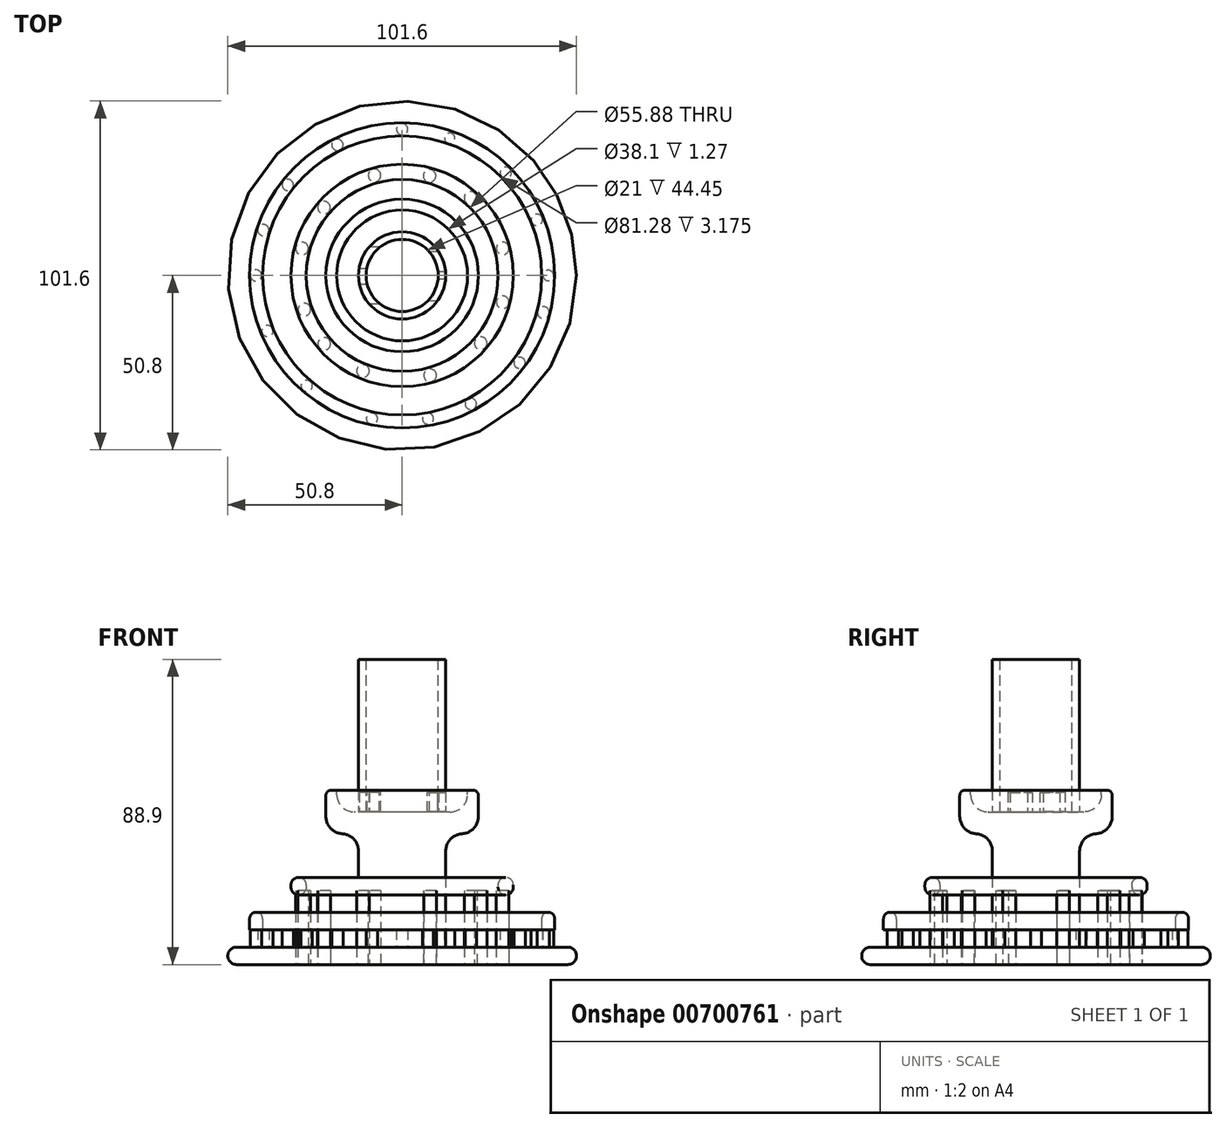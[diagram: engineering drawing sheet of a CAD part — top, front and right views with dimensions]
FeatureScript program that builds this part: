
annotation { "Feature Type Name" : "Feature", "Feature Type Description" : "" }
export const myFeature = defineFeature(function(context is Context, id is Id, definition is map)
    precondition{}
    {
        {
            var Q0;
            Q0=qCreatedBy(makeId("Top.planeOp"),FACE);
            var sketch = newSketch(context, id + "F0", { "sketchPlane" : qUnion([Q0])});
            skCircle(sketch, "E0", {"center": v(0, 0) * mm, "radius": 50.8 * mm});
            skSolve(sketch);
        }
        {
            var Q0;
            Q0 = qSketchRegion(id + "F0", true);
            extrude(context, id + "F1", {"entities" : qUnion([Q0]), "depth" : 5.08 * mm, "offsetDistance" : 25.4 * mm});
        }
        {
            var Q0;
            Q0=makeQuery(id+"F1.opExtrude","SWEPT_FACE",FACE,{"disambiguationData":[OSD([sQuery(id+"F0.wireOp",EDGE,"E0")])]});
            fillet(context, id + "F2", {"entities" : qUnion([Q0]), "radius" : 2.54 * mm, "tangentPropagation" : true, "allowEdgeOverflow" : false});
        }
        {
            var Q0;
            Q0=qCreatedBy(makeId("Top.planeOp"),FACE);
            var sketch = newSketch(context, id + "F3", { "sketchPlane" : qUnion([Q0])});
            skCircle(sketch, "E1", {"center": v(0, 0) * mm, "radius": 12.7 * mm});
            skSolve(sketch);
        }
        {
            var Q0;
            Q0 = qSketchRegion(id + "F3", true);
            extrude(context, id + "F4", {"entities" : qUnion([Q0]), "operationType" : NewBodyOperationType.ADD, "depth" : 88.9 * mm, "offsetDistance" : 25.4 * mm});
        }
        {
            var Q0;
            Q0=qCreatedBy(makeId("Top.planeOp"),FACE);
            var sketch = newSketch(context, id + "F5", { "sketchPlane" : qUnion([Q0])});
            skCircle(sketch, "E2", {"center": v(0, 0) * mm, "radius": 22.23 * mm});
            skSolve(sketch);
        }
        {
            var Q0;
            Q0 = qSketchRegion(id + "F5", true);
            extrude(context, id + "F6", {"entities" : qUnion([Q0]), "operationType" : NewBodyOperationType.ADD, "depth" : 50.8 * mm, "offsetDistance" : 25.4 * mm, "hasSecondDirection" : true, "secondDirectionOppositeDirection" : false, "secondDirectionDepth" : 38.1 * mm});
        }
        {
            var Q0;
            Q0=makeQuery(id+"F6.opExtrude","CAP_EDGE",EDGE,{"disambiguationData":[OSD([sQuery(id+"F5.wireOp",EDGE,"E2")])],"isStart":true});
            fillet(context, id + "F7", {"entities" : qUnion([Q0]), "radius" : 5.08 * mm, "tangentPropagation" : true, "allowEdgeOverflow" : false});
        }
        {
            var Q0;
            Q0=makeQuery(id+"F6.opExtrude","CAP_FACE",FACE,{"disambiguationData":[OSD([sQuery(id+"F5.wireOp",EDGE,"E2")])],"isStart":false});
            var sketch = newSketch(context, id + "F8", { "sketchPlane" : qUnion([Q0])});
            skCircle(sketch, "E3", {"center": v(0, 0) * mm, "radius": 12.7 * mm});
            skCircle(sketch, "E4", {"center": v(0, 0) * mm, "radius": 19.05 * mm});
            skSolve(sketch);
        }
        {
            var Q0;
            Q0 = qSketchRegion(id + "F8", true);
            extrude(context, id + "F9", {"entities" : qUnion([Q0]), "operationType" : NewBodyOperationType.REMOVE, "oppositeDirection" : true, "depth" : 6.35 * mm, "offsetDistance" : 25.4 * mm});
        }
        {
            var Q0;
            Q0=makeQuery(id+"F9.boolean.opBoolean","COPY",EDGE,{"derivedFrom":makeQuery(id+"F9.opExtrude","CAP_EDGE",EDGE,{"disambiguationData":[OSD([sQuery(id+"F8.wireOp",EDGE,"E4")])],"isStart":false})});
            fillet(context, id + "F10", {"entities" : qUnion([Q0]), "radius" : 5.08 * mm, "tangentPropagation" : true, "allowEdgeOverflow" : false});
        }
        {
            var Q0;
            Q0=qCreatedBy(makeId("Right.planeOp"),FACE);
            var sketch = newSketch(context, id + "F11", { "sketchPlane" : qUnion([Q0])});
            skLineSegment(sketch, "E5.bottom", {"start": v(-8.18, 44.59) * mm, "end": v(-2.47, 44.59) * mm});
            skLineSegment(sketch, "E5.top", {"start": v(-8.18, 50.22) * mm, "end": v(-2.47, 50.22) * mm});
            skLineSegment(sketch, "E5.left", {"start": v(-8.18, 44.59) * mm, "end": v(-8.18, 50.22) * mm});
            skLineSegment(sketch, "E5.right", {"start": v(-2.47, 44.59) * mm, "end": v(-2.47, 50.22) * mm});
            skLineSegment(sketch, "E6.bottom", {"start": v(2.09, 50.22) * mm, "end": v(8.4, 50.22) * mm});
            skLineSegment(sketch, "E6.top", {"start": v(2.09, 44.67) * mm, "end": v(8.4, 44.67) * mm});
            skLineSegment(sketch, "E6.left", {"start": v(2.09, 50.22) * mm, "end": v(2.09, 44.67) * mm});
            skLineSegment(sketch, "E6.right", {"start": v(8.4, 50.22) * mm, "end": v(8.4, 44.67) * mm});
            skSolve(sketch);
        }
        {
            var Q0;
            Q0 = qSketchRegion(id + "F11", true);
            extrude(context, id + "F12", {"entities" : qUnion([Q0]), "operationType" : NewBodyOperationType.REMOVE, "oppositeDirection" : true, "depth" : 12.7 * mm, "offsetDistance" : 25.4 * mm});
        }
        {
            var Q0;
            Q0=qCreatedBy(makeId("Right.planeOp"),FACE);
            var sketch = newSketch(context, id + "F13", { "sketchPlane" : qUnion([Q0])});
            skLineSegment(sketch, "E7.bottom", {"start": v(-7.5, 44.52) * mm, "end": v(-1.1, 44.52) * mm});
            skLineSegment(sketch, "E7.top", {"start": v(-7.5, 50.15) * mm, "end": v(-1.1, 50.15) * mm});
            skLineSegment(sketch, "E7.left", {"start": v(-7.5, 44.52) * mm, "end": v(-7.5, 50.15) * mm});
            skLineSegment(sketch, "E7.right", {"start": v(-1.1, 44.52) * mm, "end": v(-1.1, 50.15) * mm});
            skLineSegment(sketch, "E8.bottom", {"start": v(1.04, 50.15) * mm, "end": v(6.86, 50.15) * mm});
            skLineSegment(sketch, "E8.top", {"start": v(1.04, 44.54) * mm, "end": v(6.86, 44.54) * mm});
            skLineSegment(sketch, "E8.left", {"start": v(1.04, 50.15) * mm, "end": v(1.04, 44.54) * mm});
            skLineSegment(sketch, "E8.right", {"start": v(6.86, 50.15) * mm, "end": v(6.86, 44.54) * mm});
            skSolve(sketch);
        }
        {
            var Q0;
            Q0 = qSketchRegion(id + "F13", true);
            extrude(context, id + "F14", {"entities" : qUnion([Q0]), "operationType" : NewBodyOperationType.REMOVE, "depth" : 12.7 * mm, "offsetDistance" : 25.4 * mm});
        }
        {
            var Q0;
            Q0=makeQuery(id+"F4.opExtrude","CAP_FACE",FACE,{"disambiguationData":[OSD([sQuery(id+"F3.wireOp",EDGE,"E1")])],"isStart":false});
            var sketch = newSketch(context, id + "F15", { "sketchPlane" : qUnion([Q0])});
            skCircle(sketch, "E9", {"center": v(0, 0) * mm, "radius": 10.5 * mm});
            skSolve(sketch);
        }
        {
            var Q0;
            Q0 = qSketchRegion(id + "F15", true);
            extrude(context, id + "F16", {"entities" : qUnion([Q0]), "operationType" : NewBodyOperationType.REMOVE, "oppositeDirection" : true, "depth" : 44.45 * mm, "offsetDistance" : 25.4 * mm});
        }
        {
            var Q0;
            Q0=makeQuery(id+"F9.boolean.opBoolean","COPY",EDGE,{"derivedFrom":makeQuery(id+"F9.opExtrude","CAP_EDGE",EDGE,{"disambiguationData":[OSD([sQuery(id+"F8.wireOp",EDGE,"E4")])],"isStart":true})});
            var Q1;
            Q1=makeQuery(id+"F6.opExtrude","CAP_EDGE",EDGE,{"disambiguationData":[OSD([sQuery(id+"F5.wireOp",EDGE,"E2")])],"isStart":false});
            fillet(context, id + "F17", {"entities" : qUnion([Q0, Q1]), "radius" : 1.57 * mm, "tangentPropagation" : true, "allowEdgeOverflow" : false});
        }
        {
            var Q0;
            Q0=qCreatedBy(makeId("Top.planeOp"),FACE);
            var sketch = newSketch(context, id + "F18", { "sketchPlane" : qUnion([Q0])});
            skCircle(sketch, "E10", {"center": v(0, 0) * mm, "radius": 32.39 * mm});
            skCircle(sketch, "E11", {"center": v(0, 0) * mm, "radius": 27.94 * mm});
            skSolve(sketch);
        }
        {
            var Q0;
            Q0 = qSketchRegion(id + "F18", true);
            extrude(context, id + "F19", {"entities" : qUnion([Q0]), "depth" : 25.4 * mm, "offsetDistance" : 25.4 * mm, "hasSecondDirection" : true, "secondDirectionOppositeDirection" : false, "secondDirectionDepth" : 20.32 * mm});
        }
        {
            var Q0;
            Q0=makeQuery(id+"F19.opExtrude","CAP_EDGE",EDGE,{"disambiguationData":[OSD([sQuery(id+"F18.wireOp",EDGE,"E11")])],"isStart":false});
            var Q1;
            Q1=makeQuery(id+"F19.opExtrude","CAP_FACE",FACE,{"disambiguationData":[OSD([sQuery(id+"F18.wireOp",EDGE,"E10"),sQuery(id+"F18.wireOp",EDGE,"E11")])],"isStart":false});
            var Q2;
            Q2=makeQuery(id+"F19.opExtrude","CAP_EDGE",EDGE,{"disambiguationData":[OSD([sQuery(id+"F18.wireOp",EDGE,"E10")])],"isStart":false});
            var Q3;
            Q3=makeQuery(id+"F19.opExtrude","CAP_EDGE",EDGE,{"disambiguationData":[OSD([sQuery(id+"F18.wireOp",EDGE,"E11")])],"isStart":true});
            var Q4;
            Q4=makeQuery(id+"F19.opExtrude","CAP_EDGE",EDGE,{"disambiguationData":[OSD([sQuery(id+"F18.wireOp",EDGE,"E10")])],"isStart":true});
            fillet(context, id + "F20", {"entities" : qUnion([Q0, Q1, Q2, Q3, Q4]), "radius" : 2.22 * mm, "tangentPropagation" : true, "allowEdgeOverflow" : false});
        }
        {
            var Q0;
            Q0=qCreatedBy(makeId("Top.planeOp"),FACE);
            var sketch = newSketch(context, id + "F21", { "sketchPlane" : qUnion([Q0])});
            skCircle(sketch, "E12", {"center": v(-11.4, -27.8) * mm, "radius": 1.84 * mm});
            skCircle(sketch, "E13", {"center": v(8.15, -29.1) * mm, "radius": 1.84 * mm});
            skCircle(sketch, "E14", {"center": v(22.88, -19.7) * mm, "radius": 1.84 * mm});
            skCircle(sketch, "E15", {"center": v(-22.7, -19.9) * mm, "radius": 1.84 * mm});
            skCircle(sketch, "E16", {"center": v(29.3, -7.8) * mm, "radius": 1.84 * mm});
            skCircle(sketch, "E17", {"center": v(29.3, 7.87) * mm, "radius": 1.84 * mm});
            skCircle(sketch, "E18", {"center": v(19.9, 22.6) * mm, "radius": 1.84 * mm});
            skCircle(sketch, "E19", {"center": v(8, 29.01) * mm, "radius": 1.84 * mm});
            skCircle(sketch, "E20", {"center": v(-8.05, 29.15) * mm, "radius": 1.84 * mm});
            skCircle(sketch, "E21", {"center": v(-22.77, 19.75) * mm, "radius": 1.84 * mm});
            skCircle(sketch, "E22", {"center": v(-29.18, 7.85) * mm, "radius": 1.84 * mm});
            skCircle(sketch, "E23", {"center": v(-28.5, -9.94) * mm, "radius": 1.84 * mm});
            skSolve(sketch);
        }
        {
            var Q0;
            Q0 = qSketchRegion(id + "F21", true);
            extrude(context, id + "F22", {"entities" : qUnion([Q0]), "depth" : 21.59 * mm, "offsetDistance" : 25.4 * mm});
        }
        {
            var Q0;
            Q0=qCreatedBy(makeId("Top.planeOp"),FACE);
            var sketch = newSketch(context, id + "F23", { "sketchPlane" : qUnion([Q0])});
            skCircle(sketch, "E24", {"center": v(0, 0) * mm, "radius": 40.64 * mm});
            skCircle(sketch, "E25", {"center": v(0, 0) * mm, "radius": 44.45 * mm});
            skSolve(sketch);
        }
        {
            var Q0;
            Q0 = qSketchRegion(id + "F23", true);
            extrude(context, id + "F24", {"entities" : qUnion([Q0]), "depth" : 15.24 * mm, "offsetDistance" : 25.4 * mm, "hasSecondDirection" : true, "secondDirectionOppositeDirection" : false, "secondDirectionDepth" : 10.16 * mm});
        }
        {
            var Q0;
            Q0=makeQuery(id+"F24.opExtrude","CAP_EDGE",EDGE,{"disambiguationData":[OSD([sQuery(id+"F23.wireOp",EDGE,"E24")])],"isStart":false});
            var Q1;
            Q1=makeQuery(id+"F24.opExtrude","CAP_EDGE",EDGE,{"disambiguationData":[OSD([sQuery(id+"F23.wireOp",EDGE,"E25")])],"isStart":false});
            fillet(context, id + "F25", {"entities" : qUnion([Q0, Q1]), "radius" : 1.9 * mm, "tangentPropagation" : true, "allowEdgeOverflow" : false});
        }
        {
            var Q0;
            Q0=qCreatedBy(makeId("Top.planeOp"),FACE);
            var sketch = newSketch(context, id + "F26", { "sketchPlane" : qUnion([Q0])});
            skCircle(sketch, "E26", {"center": v(-18.86, 38.03) * mm, "radius": 1.65 * mm});
            skCircle(sketch, "E27", {"center": v(0, 42.6) * mm, "radius": 1.65 * mm});
            skCircle(sketch, "E28", {"center": v(-33.32, 26.35) * mm, "radius": 1.65 * mm});
            skCircle(sketch, "E29", {"center": v(-40.45, 13.2) * mm, "radius": 1.65 * mm});
            skCircle(sketch, "E30", {"center": v(-42.6, 0) * mm, "radius": 1.65 * mm});
            skCircle(sketch, "E31", {"center": v(-39.26, -16.16) * mm, "radius": 1.65 * mm});
            skCircle(sketch, "E32", {"center": v(-27.8, -32.16) * mm, "radius": 1.65 * mm});
            skCircle(sketch, "E33", {"center": v(-8.8, -41.71) * mm, "radius": 1.65 * mm});
            skCircle(sketch, "E34", {"center": v(19.99, -37.4) * mm, "radius": 1.65 * mm});
            skCircle(sketch, "E35", {"center": v(34.2, -25.44) * mm, "radius": 1.65 * mm});
            skCircle(sketch, "E36", {"center": v(13.86, 39.93) * mm, "radius": 1.52 * mm});
            skCircle(sketch, "E37", {"center": v(30.18, 29.92) * mm, "radius": 1.65 * mm});
            skCircle(sketch, "E38", {"center": v(39.24, 16.19) * mm, "radius": 1.67 * mm});
            skCircle(sketch, "E39", {"center": v(42.6, 0) * mm, "radius": 1.55 * mm});
            skCircle(sketch, "E40", {"center": v(41.12, -10.77) * mm, "radius": 1.72 * mm});
            skCircle(sketch, "E41", {"center": v(7.52, -41.7) * mm, "radius": 1.62 * mm});
            skSolve(sketch);
        }
        {
            var Q0;
            Q0 = qSketchRegion(id + "F26", true);
            extrude(context, id + "F27", {"entities" : qUnion([Q0]), "depth" : 10.16 * mm, "offsetDistance" : 25.4 * mm, "hasSecondDirection" : true, "secondDirectionOppositeDirection" : false, "secondDirectionDepth" : 5.08 * mm});
        }
        {
            var Q0;
            Q0=makeQuery(id+"F6.boolean.opBoolean","INTERSECT",EDGE,{"derivedFrom":[makeQuery(id+"F4.opExtrude","SWEPT_FACE",FACE,{"disambiguationData":[OSD([sQuery(id+"F3.wireOp",EDGE,"E1")])]}),makeQuery(id+"F6.opExtrude","CAP_FACE",FACE,{"disambiguationData":[OSD([sQuery(id+"F5.wireOp",EDGE,"E2")])],"isStart":true})]});
            fillet(context, id + "F28", {"entities" : qUnion([Q0]), "radius" : 5.08 * mm, "tangentPropagation" : true, "allowEdgeOverflow" : false});
        }
    });
